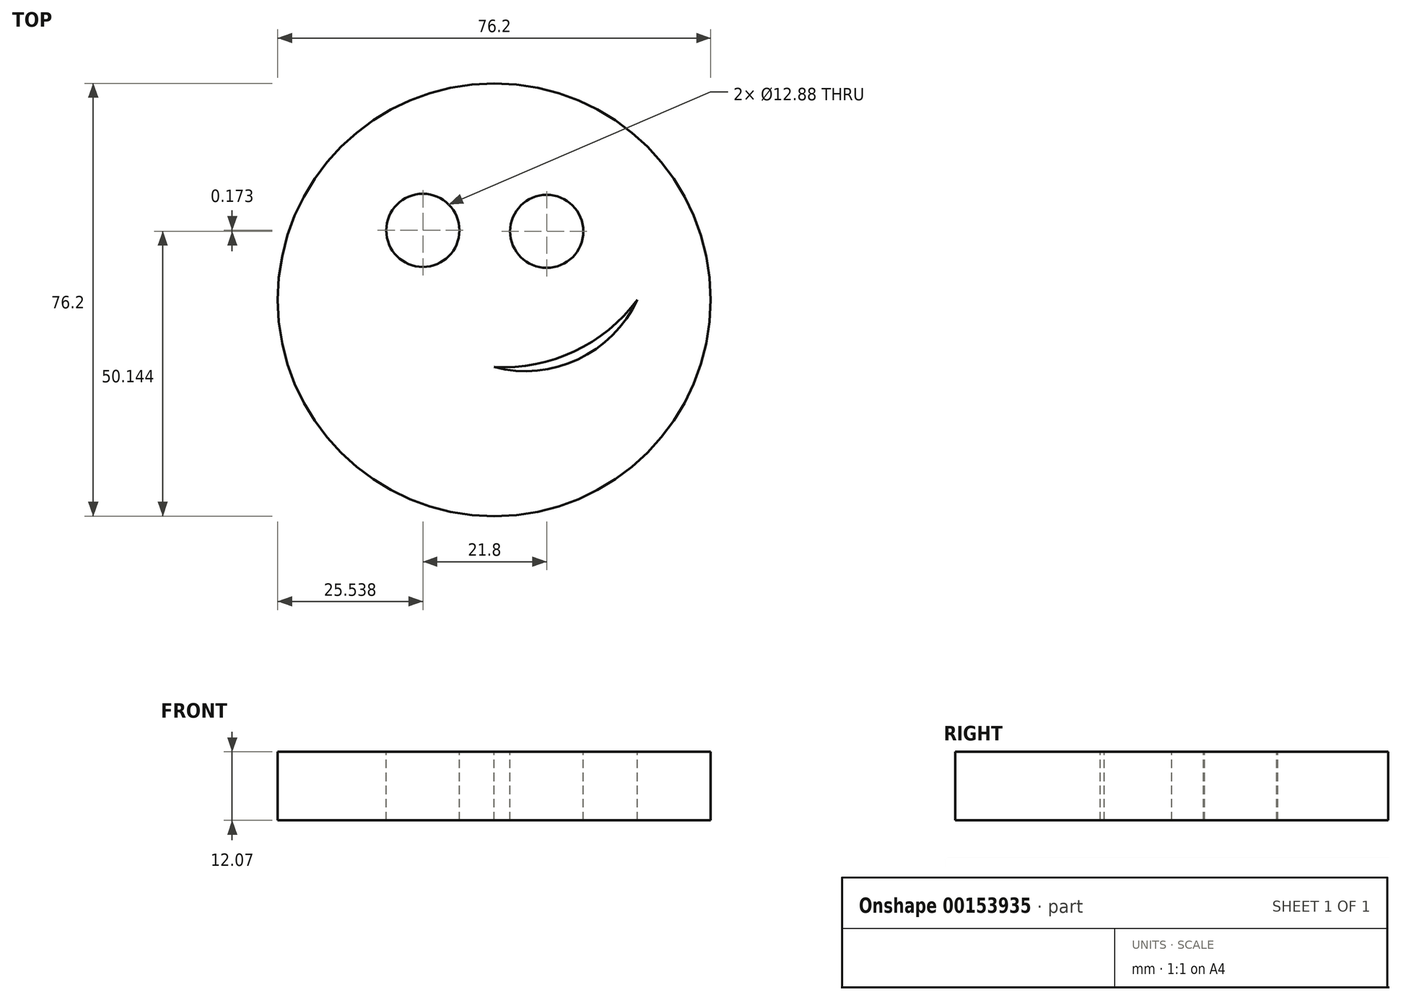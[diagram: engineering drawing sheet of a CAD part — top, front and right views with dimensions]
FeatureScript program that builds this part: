
annotation { "Feature Type Name" : "Feature", "Feature Type Description" : "" }
export const myFeature = defineFeature(function(context is Context, id is Id, definition is map)
    precondition{}
    {
        {
            var Q0;
            Q0=qCreatedBy(makeId("Top.planeOp"),FACE);
            var sketch = newSketch(context, id + "F0", { "sketchPlane" : qUnion([Q0])});
            skCircle(sketch, "E0", {"center": v(0, 0) * mm, "radius": 38.1 * mm});
            skSolve(sketch);
        }
        {
            var Q0;
            Q0 = qSketchRegion(id + "F0", true);
            extrude(context, id + "F1", {"entities" : qUnion([Q0]), "depth" : 12.06 * mm});
        }
        {
            var Q0;
            Q0=makeQuery(id+"F1.opExtrude","CAP_FACE",FACE,{"disambiguationData":[OSD([sQuery(id+"F0.wireOp",EDGE,"E0")])],"isStart":false});
            var sketch = newSketch(context, id + "F2", { "sketchPlane" : qUnion([Q0])});
            skCircle(sketch, "E1", {"center": v(-12.56, 12.22) * mm, "radius": 6.44 * mm});
            skCircle(sketch, "E2", {"center": v(9.24, 12.04) * mm, "radius": 6.44 * mm});
            skArc(sketch, "E3", {"start": v(0, -11.86) * mm, "mid": v(14.75, -10.5) * mm, "end": v(25.2, 0) * mm});
            skArc(sketch, "E4", {"start": v(0, -11.86) * mm, "mid": v(14.09, -9.09) * mm, "end": v(25.2, 0) * mm});
            skSolve(sketch);
        }
        {
            var Q0;
            Q0 = qSketchRegion(id + "F2", true);
            extrude(context, id + "F3", {"entities" : qUnion([Q0]), "operationType" : NewBodyOperationType.REMOVE, "oppositeDirection" : true, "depth" : 25.4 * mm});
        }
    });
